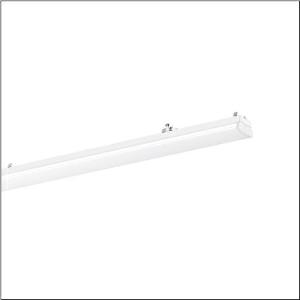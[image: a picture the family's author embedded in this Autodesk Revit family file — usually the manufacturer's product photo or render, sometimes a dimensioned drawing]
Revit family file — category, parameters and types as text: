
# Revit family: licross_r__21_recessed_opal_ho_52tl1ddv4l2m_f78d
name_source: partatom
category: Lighting Fixtures
units: mm (PartAtom-declared; Revit-internal decimal feet)

## family parameters
Cut with Voids When Loaded = No
Host = Face
Light Source = No
Part Type = Normal
Room Calculation Point = No
Round Connector Dimension = Use Diameter
Shared = No

## types (1)
- --- (1 x LED, 22050 lm, 125.6 W, 4000K)
    Apparent Load = 126 VA
    CIE Flux Codes = 44 73 91 87 100
    Color Rendering = 80
    Color Temperature = 4000K
    Default Elevation = 1800 mm
    Description = Licross® 21 recessed opal HO, luminaire insert, of sheet steel, galvanised, coil coated, white, length: 2.250mm, width: 66mm, height: 67mm, LED rated luminous flux: 22.050lm, light colour: 840, control gear: DALI 2, with plug, 5-pole, with phase selection, mains connection: 220..240V, AC, 50/60Hz, rated input power: 126W, halogen-free wiring, primary optical cover: cover, of PMMA, light emission: direct with ceiling illumination distribution, primary light characteristic: symmetric, protection rating (complete): IP40, insulation class (complete): insulation class I (protective earthing), certification: CE, ENEC, VDE, UKCA, protection symbol: D if used in an environment without relevant dust loads with corresponding accessories, impact resistance: IK06, permissible ambient temperature for indoor applications: -40..+30°C, corresponds to IFS (International Featured Standards) requirements for safety and quality in the food industry, reducing of maximum allowable ambient temperature of 5°C with ceiling mounting, LABS conformity tested according to VDMA 24364:2018-05, packaging unit: 1 piece
    Height = 83 mm
    Lamp = 1 x LED
    Lamp Light Flux = 22050 lm
    Lamp Power = 125.6 W
    Lamp count = 1
    Length = 2250 mm
    Luminous efficacy = 176 lm/W
    Manufacturer = Siteco
    ModVariant = No
    Model = 52TL1DDV4L2M
    Mounting Place = Ceiling
    Mounting Type = Pendant
    Number of Poles = 1
    OnlyDefault = Yes
    Power Factor = 1
    Product Name = Licross® 21 recessed opal HO
    Product group = luminaire insert
    ProductGroupID = 901
    Protection Class = Protection class I
    Protection Degree = IP 40
    RLX_Detail_Level = 1
    RLX_Emergency_Light_Flux = 0 lm
    RLX_Emergency_Type = 0
    RLX_Emergency_Type_DB = No
    RlxData = <blob elided: 26893 chars, md5=2ddaf562>
    Socket = socket
    Standby Power = 0 W
    System Light Flux = 22050 lm
    System Power = 126 W
    Type Comments = factory setting: luminous flux: 100 % | dim-lin: 254 | 489 mA
    Type Image = l_1313666.jpg
    URL = http://relux.com
    VarID = @adj_023425
    Voltage = 0 V
    Weight = 0.00 kg
    Width = 76 mm

## geometry (parser evidence)
native form markers: Blend x4, Sweep x14
no freeform markers — native parametric forms only
